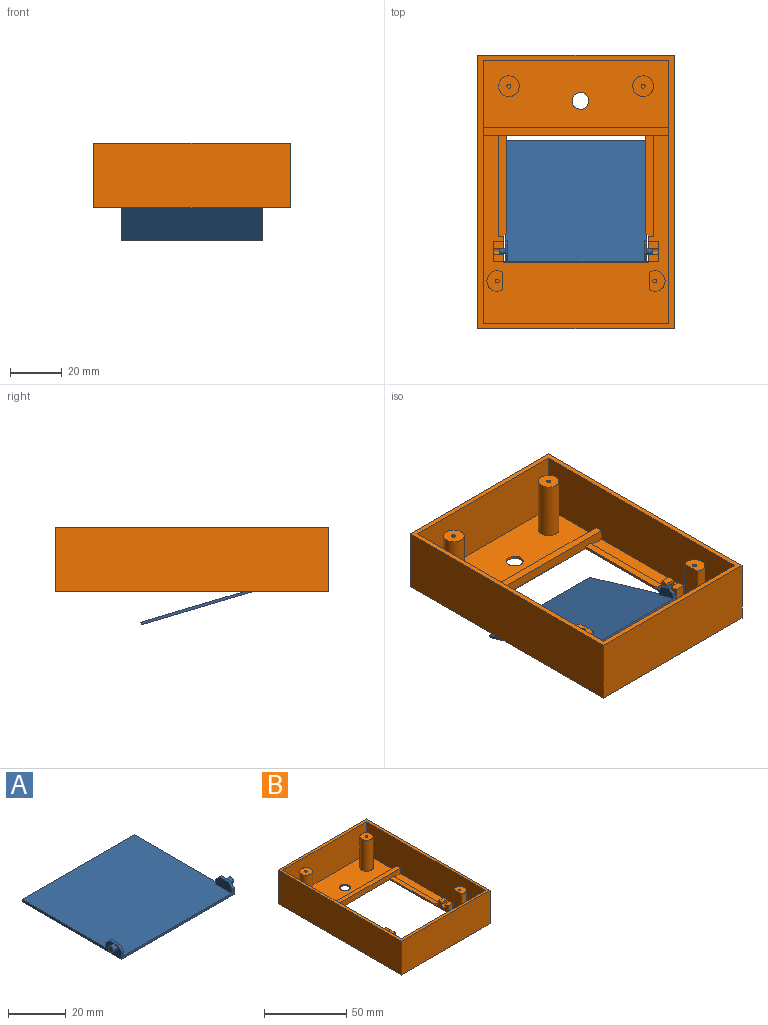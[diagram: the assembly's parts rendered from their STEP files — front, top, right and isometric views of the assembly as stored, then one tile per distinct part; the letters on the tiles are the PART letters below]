
ASSEMBLY  parts=2 mates=1
PART A: 20 faces, bbox 59x49x5 mm
  f0: plane 55x49mm, normal (0,0,1), area 2679mm2, adj f1,f2,f3,f4,f6,f7,f11,f12
  f1: plane 55x3mm, normal (0,-1,0), area 59mm2, adj f0,f2,f4,f5,f7,f12,f16,f18
  f2: plane 49x5mm, normal (1,0,0), area 72.5mm2, adj f0,f1,f3,f5,f11,f13,f14,f16
  f3: plane 55x1mm, normal (0,1,0), area 55mm2, adj f0,f2,f4,f5
  f4: plane 49x5mm, normal (-1,0,0), area 72.5mm2, adj f0,f1,f3,f5,f6,f8,f9,f18
  f5: plane 55x49mm, normal (0,0,-1), area 2695mm2, adj f1,f2,f3,f4
  f6: plane 2x1mm, normal (0,1,0), area 2mm2, adj f0,f4,f7,f19
  f7: plane 8x4mm, normal (1,0,0), area 28mm2, adj f0,f1,f6,f8,f18,f19
  f8: plane 4x1mm, normal (0,0,1), area 4mm2, adj f4,f7,f18,f19
  f9: cylinder r=1.2mm len=2.4mm, axis (1,0,0), area 15.1mm2, adj f4,f10
  f10: plane 2.4x2.4mm, normal (-1,0,0), area 4.5mm2, adj f9
  f11: plane 2x1mm, normal (0,1,0), area 2mm2, adj f0,f2,f12,f17
  f12: plane 8x4mm, normal (-1,0,0), area 28mm2, adj f0,f1,f11,f13,f16,f17
  f13: plane 4x1mm, normal (0,0,1), area 4mm2, adj f2,f12,f16,f17
  f14: cylinder r=1.2mm len=2.4mm, axis (-1,0,0), area 15.1mm2, adj f2,f15
  f15: plane 2.4x2.4mm, normal (1,0,0), area 4.5mm2, adj f14
  f16: plane 2x2mm, normal (0,-0.71,0.71), area 2.8mm2, adj f1,f2,f12,f13
  f17: plane 2x2mm, normal (0,0.71,0.71), area 2.8mm2, adj f2,f11,f12,f13
  f18: plane 2x2mm, normal (0,-0.71,0.71), area 2.8mm2, adj f1,f4,f7,f8
  f19: plane 2x2mm, normal (0,0.71,0.71), area 2.8mm2, adj f4,f6,f7,f8
PART B: 66 faces, bbox 76x106x25 mm
  f0: plane 72x4mm, normal (0,-1,0), area 282mm2, adj f1,f3,f16,f52,f53,f56,f58,f59
  f1: plane 73x72mm, normal (0,0,1), area 2181.6mm2, adj f0,f3,f8,f14,f16,f17,f18,f22
  f2: plane 72x26mm, normal (0,0,1), area 1738.3mm2, adj f3,f15,f16,f27,f31,f51,f55
  f3: plane 102x24mm, normal (-1,0,0), area 2436mm2, adj f0,f1,f2,f9,f14,f15,f51,f52
  f4: plane 106x76mm, normal (0,0,-1), area 5221.5mm2, adj f8,f10,f11,f12,f13,f43,f49,f50
  f5: plane 4x2.74mm, normal (0,0,1), area 11mm2, adj f43,f44,f45,f47
  f6: cylinder r=1.5mm len=4mm, axis (-1,0,0), area 25.7mm2, adj f43,f45,f47,f48
  f7: plane 4x2.74mm, normal (0,0,1), area 11mm2, adj f8,f35,f36,f40
  f8: plane 50.5x5.5mm, normal (1,0,0), area 77.3mm2, adj f1,f4,f7,f35,f37,f38,f39,f40
  f9: plane 106x76mm, normal (0,0,1), area 712mm2, adj f3,f10,f11,f12,f13,f14,f15,f16
  f10: plane 76x25mm, normal (0,-1,0), area 1900mm2, adj f4,f9,f11,f13
  f11: plane 106x25mm, normal (1,0,0), area 2650mm2, adj f4,f9,f10,f12
  f12: plane 76x25mm, normal (0,1,0), area 1900mm2, adj f4,f9,f11,f13
  f13: plane 106x25mm, normal (-1,0,0), area 2650mm2, adj f4,f9,f10,f12
  f14: plane 72x24mm, normal (0,1,0), area 1728mm2, adj f1,f3,f9,f16
  f15: plane 72x24mm, normal (0,-1,0), area 1728mm2, adj f2,f3,f9,f16
  f16: plane 102x24mm, normal (1,0,0), area 2436mm2, adj f0,f1,f2,f9,f14,f15,f51,f52
  f17: plane 18.5x6.93mm, normal (1,0,0), area 128.2mm2, adj f1,f18,f19
  f18: cylinder r=4mm len=18.5mm, axis (0,0,-1), area 310mm2, adj f1,f17,f19
  f19: plane 8x6mm, normal (0,0,1), area 38.7mm2, adj f17,f18,f20
  f20: cylinder r=0.75mm len=15mm, axis (0,0,1), area 70.7mm2, adj f19,f21
  f21: plane 1.5x1.5mm, normal (0,0,1), area 1.8mm2, adj f20
  f22: plane 18.5x6.93mm, normal (-1,0,0), area 128.2mm2, adj f1,f23,f24
  f23: cylinder r=4mm len=18.5mm, axis (0,0,-1), area 310mm2, adj f1,f22,f24
  f24: plane 8x6mm, normal (0,0,1), area 38.7mm2, adj f22,f23,f25
  f25: cylinder r=0.75mm len=15mm, axis (0,0,1), area 70.7mm2, adj f24,f26
  f26: plane 1.5x1.5mm, normal (0,0,1), area 1.8mm2, adj f25
  f27: cylinder r=4mm len=23mm, axis (0,0,-1), area 578.1mm2, adj f2,f28
  f28: plane 8x8mm, normal (0,0,1), area 48.3mm2, adj f27,f29
  f29: cylinder r=0.8mm len=15mm, axis (0,0,1), area 75.4mm2, adj f28,f30
  f30: plane 1.6x1.6mm, normal (0,0,1), area 2mm2, adj f29
  f31: cylinder r=4mm len=23mm, axis (0,0,-1), area 578.1mm2, adj f2,f32
  f32: plane 8x8mm, normal (0,0,1), area 48.3mm2, adj f31,f33
  f33: cylinder r=0.8mm len=15mm, axis (0,0,1), area 75.4mm2, adj f32,f34
  f34: plane 1.6x1.6mm, normal (0,0,1), area 2mm2, adj f33
  f35: plane 4.5x4mm, normal (0,1,0), area 18mm2, adj f1,f7,f8,f36
  f36: plane 8x4.5mm, normal (-1,0,0), area 27.2mm2, adj f1,f7,f35,f37,f38,f39,f40,f41
  f37: plane 4.5x4mm, normal (0,-1,0), area 18mm2, adj f1,f8,f36,f38
  f38: plane 4x2.74mm, normal (0,0,1), area 11mm2, adj f8,f36,f37,f41
  f39: cylinder r=1.5mm len=4mm, axis (1,0,0), area 25.7mm2, adj f8,f36,f40,f41
  f40: plane 4x1.19mm, normal (0,-1,0), area 4.8mm2, adj f7,f8,f36,f39
  f41: plane 4x1.19mm, normal (0,1,0), area 4.8mm2, adj f8,f36,f38,f39
  f42: plane 4.5x4mm, normal (0,1,0), area 18mm2, adj f1,f43,f45,f46
  f43: plane 50.5x5.5mm, normal (-1,0,0), area 77.3mm2, adj f1,f4,f5,f6,f42,f44,f46,f47
  f44: plane 4.5x4mm, normal (0,-1,0), area 18mm2, adj f1,f5,f43,f45
  f45: plane 8x4.5mm, normal (1,0,0), area 27.2mm2, adj f1,f5,f6,f42,f44,f46,f47,f48
  f46: plane 4x2.74mm, normal (0,0,1), area 11mm2, adj f42,f43,f45,f48
  f47: plane 4x1.19mm, normal (0,1,0), area 4.8mm2, adj f5,f6,f43,f45
  f48: plane 4x1.19mm, normal (0,-1,0), area 4.8mm2, adj f6,f43,f45,f46
  f49: plane 56.03x0.5mm, normal (0,1,0), area 28mm2, adj f4,f8,f43,f54
  f50: plane 56.03x1mm, normal (0,-1,0), area 56mm2, adj f4,f8,f43,f53
  f51: plane 72x4mm, normal (0,1,0), area 288mm2, adj f2,f3,f16,f52
  f52: plane 72x3mm, normal (0,0,1), area 216mm2, adj f0,f3,f16,f51
  f53: plane 56.03x40.05mm, normal (0,0,-1), area 133.1mm2, adj f0,f8,f43,f50,f58,f60,f61,f65
  f54: plane 56.03x0.5mm, normal (0,0.71,0.71), area 39.6mm2, adj f1,f8,f43,f49
  f55: cylinder r=3.25mm len=6.5mm, axis (0,0,1), area 20.4mm2, adj f2,f4
  f56: plane 39.05x1mm, normal (-1,0,0), area 39.1mm2, adj f0,f1,f57,f59
  f57: plane 2x1mm, normal (0,-1,0), area 2mm2, adj f1,f56,f59,f60
  f58: plane 38.05x1mm, normal (1,0,0), area 38.1mm2, adj f0,f53,f59,f60
  f59: plane 39.05x3mm, normal (0,0,1), area 116.7mm2, adj f0,f56,f57,f58,f60
  f60: plane 1x1mm, normal (0.71,-0.71,0), area 1.4mm2, adj f53,f57,f58,f59
  f61: plane 38.05x1mm, normal (-1,0,0), area 38.1mm2, adj f0,f53,f64,f65
  f62: plane 2x1mm, normal (0,-1,0), area 2mm2, adj f1,f63,f64,f65
  f63: plane 39.05x1mm, normal (1,0,0), area 39.1mm2, adj f0,f1,f62,f64
  f64: plane 39.05x3mm, normal (0,0,1), area 116.7mm2, adj f0,f61,f62,f63,f65
  f65: plane 1x1mm, normal (-0.71,-0.71,0), area 1.4mm2, adj f53,f61,f62,f64
PLACE A rot(axis=(-1,0,0),16.6deg) t=(-7.5,-0.19,-6.34)mm
PLACE B t=(-7.48,3.68,-0.49)mm fixed
MATE revolute B.f6 <-> A.f9  axis (1,0,0) through (-35.5,-19.32,3.01)mm
